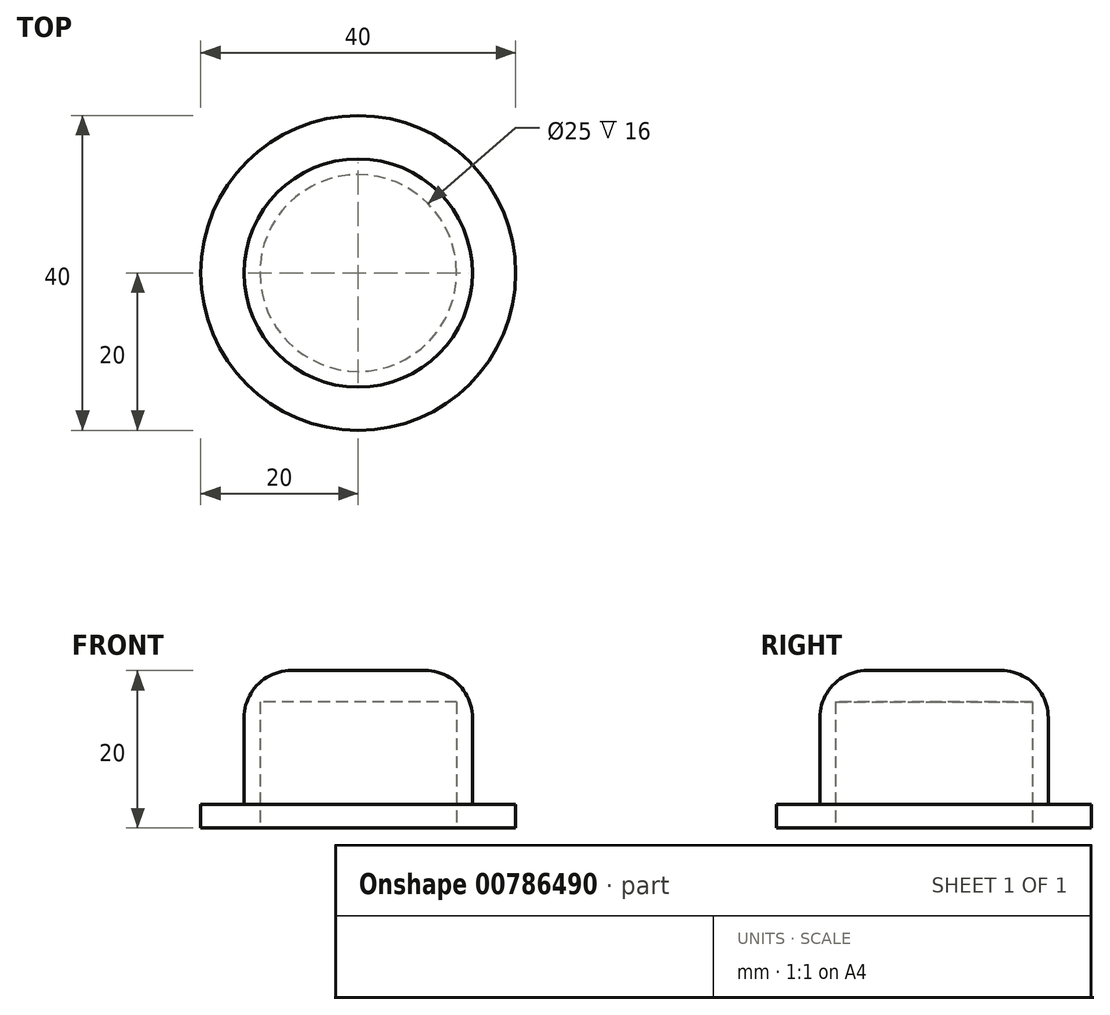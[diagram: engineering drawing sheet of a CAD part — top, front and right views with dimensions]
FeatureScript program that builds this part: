
annotation { "Feature Type Name" : "Feature", "Feature Type Description" : "" }
export const myFeature = defineFeature(function(context is Context, id is Id, definition is map)
    precondition{}
    {
        {
            var Q0;
            Q0=qCreatedBy(makeId("Top.planeOp"),FACE);
            var sketch = newSketch(context, id + "F0", { "sketchPlane" : qUnion([Q0])});
            skCircle(sketch, "E0", {"center": v(0, 0) * mm, "radius": 20 * mm});
            skCircle(sketch, "E1", {"center": v(0, 0) * mm, "radius": 14.5 * mm});
            skCircle(sketch, "E2", {"center": v(0, 0) * mm, "radius": 12.5 * mm});
            skSolve(sketch);
        }
        {
            var Q0;
            Q0 = qSketchRegion(id + "F0", true);
            extrude(context, id + "F1", {"entities" : qUnion([Q0]), "depth" : 3 * mm, "offsetDistance" : 25 * mm});
        }
        {
            var Q0;
            Q0=makeQuery(id+"F0.imprint","IMPRINT",FACE,{"disambiguationData":[TD([[makeQuery(id+"F0.imprint","IMPRINT",EDGE,{"derivedFrom":sQuery(id+"F0.wireOp",EDGE,"E1")}),1.0]])]});
            extrude(context, id + "F2", {"entities" : qUnion([Q0]), "operationType" : NewBodyOperationType.ADD, "depth" : 20 * mm, "offsetDistance" : 25 * mm});
        }
        {
            var Q0;
            Q0=makeQuery(id+"F2.opExtrude","CAP_FACE",FACE,{"disambiguationData":[OSD([sQuery(id+"F0.wireOp",EDGE,"E1"),sQuery(id+"F0.wireOp",EDGE,"E2")])],"isStart":false});
            var sketch = newSketch(context, id + "F3", { "sketchPlane" : qUnion([Q0])});
            skCircle(sketch, "E3", {"center": v(0, 0) * mm, "radius": 13.01 * mm});
            skSolve(sketch);
        }
        {
            var Q0;
            Q0 = qSketchRegion(id + "F3", true);
            extrude(context, id + "F4", {"entities" : qUnion([Q0]), "operationType" : NewBodyOperationType.ADD, "oppositeDirection" : true, "depth" : 4 * mm, "offsetDistance" : 25 * mm});
        }
        {
            var Q0;
            Q0=makeQuery(id+"F2.opExtrude","CAP_EDGE",EDGE,{"disambiguationData":[OSD([sQuery(id+"F0.wireOp",EDGE,"E1")])],"isStart":false});
            fillet(context, id + "F5", {"entities" : qUnion([Q0]), "radius" : 6 * mm, "tangentPropagation" : true, "allowEdgeOverflow" : false});
        }
    });
